# Revit family: Faucet-Delta-TALBOT-Single_Handle_Pull-Down_Kitchen_Faucet_with_Soap_Dispenser_Center_Mount
name_source: partatom
category: Plumbing Fixtures
revit_build: Autodesk Revit Architecture 2014 (Build: 20140709_2115(x64)
units: mm (PartAtom-declared; Revit-internal decimal feet)

## types (3) — shared parameters
ADA Compliant = Yes
Actual Valve Water Flow = 2 GPM
CWC R = 0"
Cold Water Connection = 0"
Default Elevation = 3' - 9 1/4"
Depth = 0' - 4 15/16"
Description = Talbott - Single Handle Pull-Down Kitchen Faucet with Soap Dispenser
Flow Rate = 2.20 gpm @ 60 psi | 8.3 L/min @ 414 kPa

Read more: http://www.deltafaucet.com
HWC R = 0"
Height = 0' - 6 5/8"
Hot Water Connection = 0"
Manufacturer = DELTA
Product Documentation Link = http://www.deltafaucet.com
Product Page URL = http://www.deltafaucet.com
Series = Talbott
URL = http://www.deltafaucet.com
Warranty URL = http://www.deltafaucet.com
Width = 0' - 6 5/8"

## per-type parameters (varying)
| type | Finish | Product Name |
| 16968-SD-DST | Chrome - DELTA - Polished | Single Handle Pull-Down Kitchen Faucet with Soap Dispenser |
| 16968-RBSD-DST | Venetian - Delta - Bronze | Single Handle Pull-Down Kitchen Faucet with Soap Dispenser

Read more: http://www.deltafaucet.com |
| 16968-SSSD-DST | Steel - DELTA - Brilliance Stainless | Single Handle Pull-Down Kitchen Faucet with Soap Dispenser

Read more: http://www.deltafaucet.com |

note: column(s) folded — value = type name in every type: Model

## geometry (parser evidence)
native form markers: Blend x12, Sweep x1
no freeform markers — native parametric forms only
